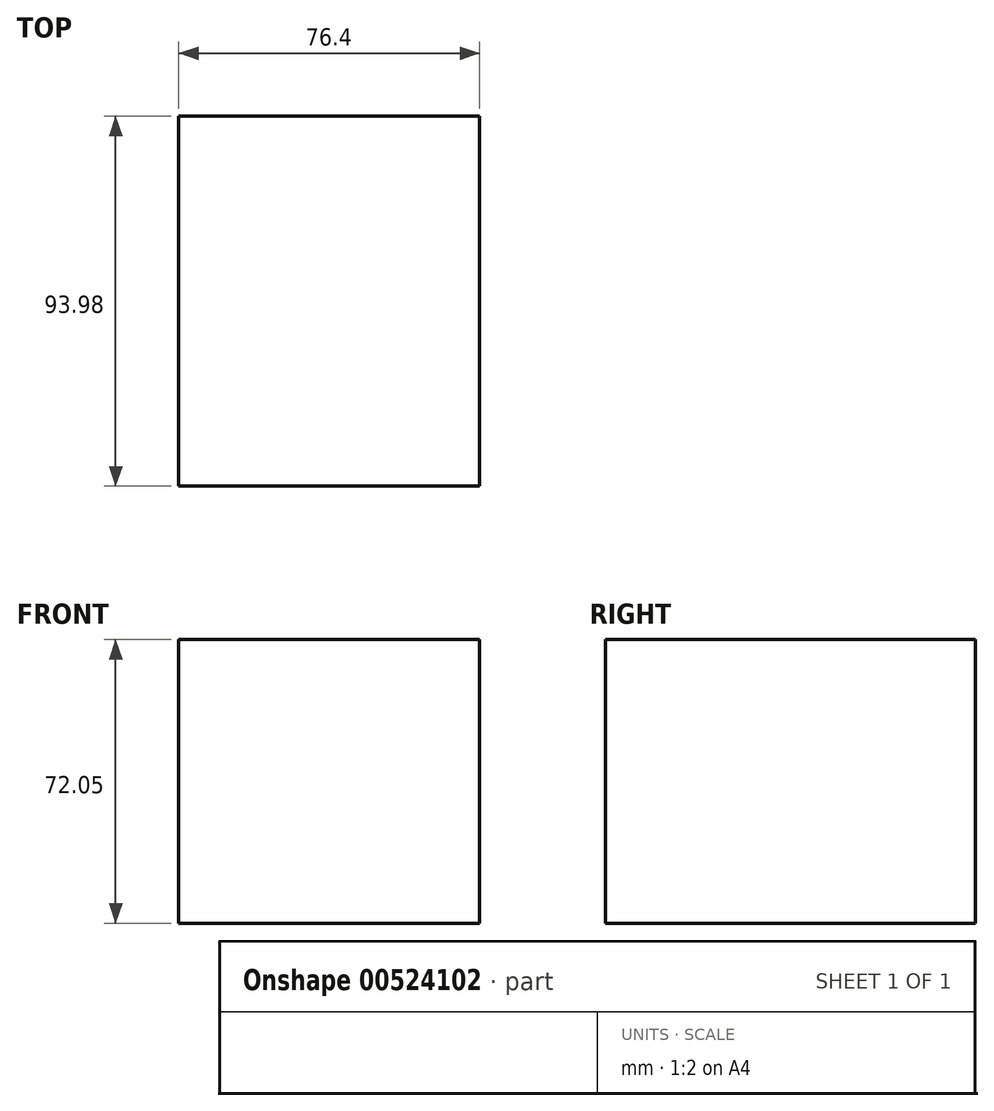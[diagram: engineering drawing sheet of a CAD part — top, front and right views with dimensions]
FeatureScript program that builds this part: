
annotation { "Feature Type Name" : "Feature", "Feature Type Description" : "" }
export const myFeature = defineFeature(function(context is Context, id is Id, definition is map)
    precondition{}
    {
        {
            var Q0;
            Q0=qCreatedBy(makeId("Front.planeOp"),FACE);
            var sketch = newSketch(context, id + "F0", { "sketchPlane" : qUnion([Q0])});
            skLineSegment(sketch, "E0.bottom", {"start": v(-35.67, 34.94) * mm, "end": v(40.73, 34.94) * mm});
            skLineSegment(sketch, "E0.top", {"start": v(-35.67, -37.11) * mm, "end": v(40.73, -37.11) * mm});
            skLineSegment(sketch, "E0.left", {"start": v(-35.67, 34.94) * mm, "end": v(-35.67, -37.11) * mm});
            skLineSegment(sketch, "E0.right", {"start": v(40.73, 34.94) * mm, "end": v(40.73, -37.11) * mm});
            skSolve(sketch);
        }
        {
            var Q0;
            Q0=makeQuery(id+"F0.imprint","IMPRINT",FACE,{"disambiguationData":[TD([[makeQuery(id+"F0.imprint","IMPRINT",EDGE,{"derivedFrom":sQuery(id+"F0.wireOp",EDGE,"E0.bottom")}),-1.0]])]});
            extrude(context, id + "F1", {"entities" : qUnion([Q0]), "depth" : 93.98 * mm, "offsetDistance" : 25.4 * mm});
        }
    });
